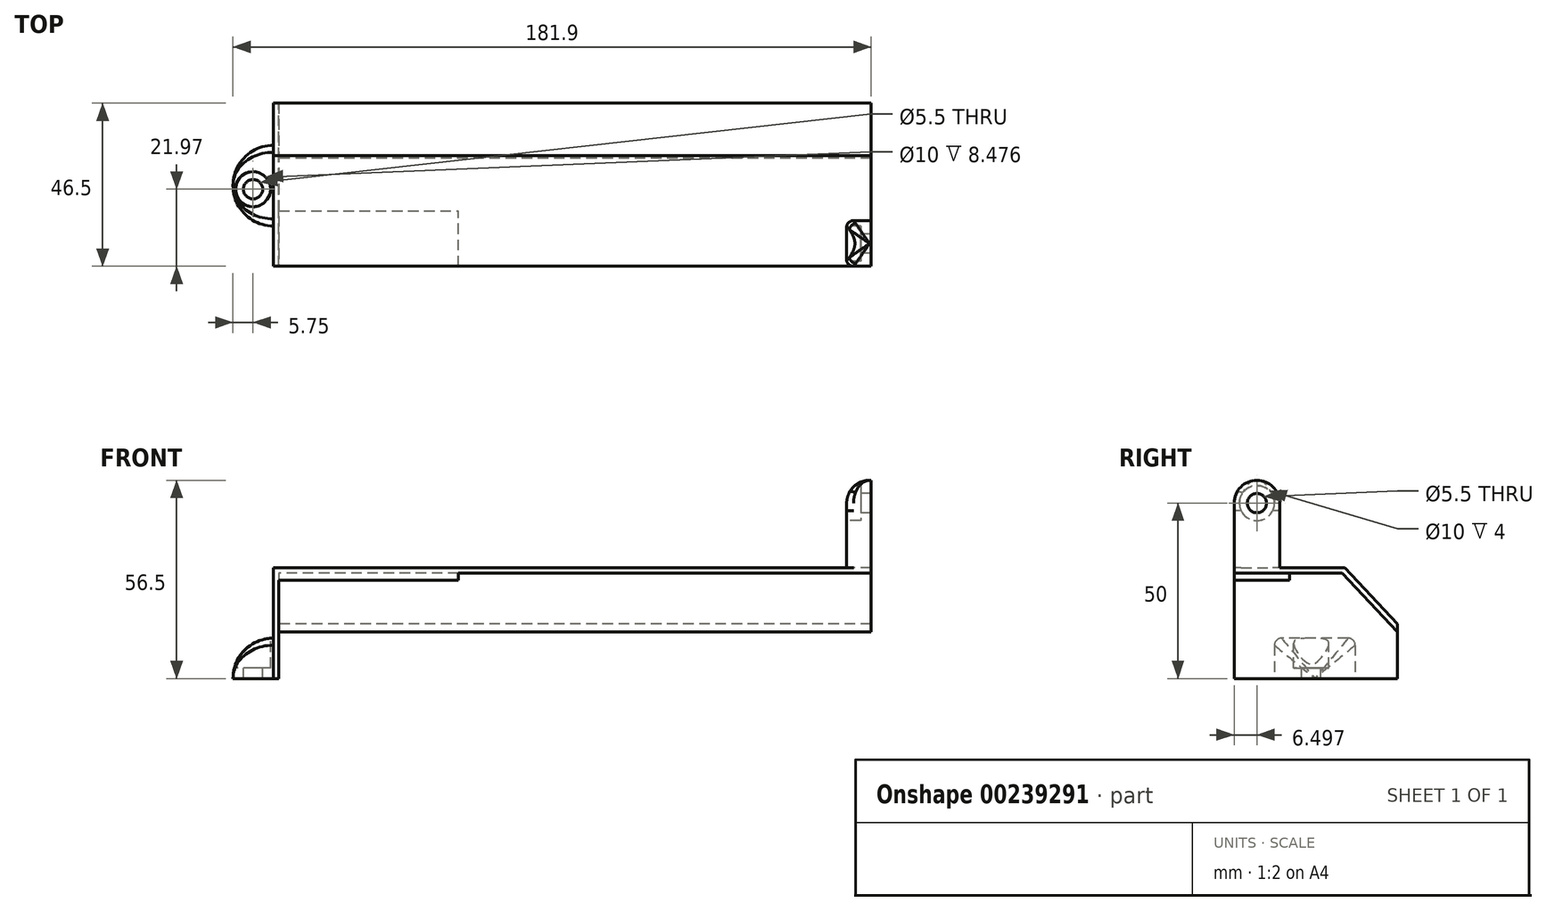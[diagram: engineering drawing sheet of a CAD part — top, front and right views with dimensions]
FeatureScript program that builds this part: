
annotation { "Feature Type Name" : "Feature", "Feature Type Description" : "" }
export const myFeature = defineFeature(function(context is Context, id is Id, definition is map)
    precondition{}
    {
        {
            var Q0;
            Q0=qCreatedBy(makeId("Right.planeOp"),FACE);
            var sketch = newSketch(context, id + "F0", { "sketchPlane" : qUnion([Q0])});
            skLineSegment(sketch, "E0", {"start": v(-21.97, 0) * mm, "end": v(-21.97, 31.6) * mm});
            skLineSegment(sketch, "E1", {"start": v(-21.97, 31.6) * mm, "end": v(-6.47, 31.6) * mm});
            skLineSegment(sketch, "E2", {"start": v(-6.47, 31.6) * mm, "end": v(9.53, 31.6) * mm});
            skLineSegment(sketch, "E3", {"start": v(9.53, 31.6) * mm, "end": v(24.53, 15.6) * mm});
            skLineSegment(sketch, "E4", {"start": v(24.53, 15.6) * mm, "end": v(24.53, 0) * mm});
            skLineSegment(sketch, "E5", {"start": v(24.53, 0) * mm, "end": v(-21.97, 0) * mm});
            skSolve(sketch);
        }
        {
            var Q0;
            Q0=makeQuery(id+"F0.imprint","IMPRINT",FACE,{"disambiguationData":[TD([[makeQuery(id+"F0.imprint","IMPRINT",EDGE,{"derivedFrom":sQuery(id+"F0.wireOp",EDGE,"E0")}),-1.0]])]});
            extrude(context, id + "F1", {"entities" : qUnion([Q0]), "depth" : 170.4 * mm});
        }
        {
            var Q0;
            Q0=makeQuery(id+"F1.opExtrude","SWEPT_FACE",FACE,{"disambiguationData":[OSD([sQuery(id+"F0.wireOp",EDGE,"E5")])]});
            var Q1;
            Q1=makeQuery(id+"F1.opExtrude","SWEPT_FACE",FACE,{"disambiguationData":[OSD([sQuery(id+"F0.wireOp",EDGE,"E4")])]});
            var Q2;
            Q2=makeQuery(id+"F1.opExtrude","SWEPT_FACE",FACE,{"disambiguationData":[OSD([sQuery(id+"F0.wireOp",EDGE,"E0")])]});
            var Q3;
            Q3=makeQuery(id+"F1.opExtrude","CAP_FACE",FACE,{"disambiguationData":[OSD([sQuery(id+"F0.wireOp",EDGE,"E0"),sQuery(id+"F0.wireOp",EDGE,"E1"),sQuery(id+"F0.wireOp",EDGE,"E2"),sQuery(id+"F0.wireOp",EDGE,"E3"),sQuery(id+"F0.wireOp",EDGE,"E4"),sQuery(id+"F0.wireOp",EDGE,"E5")])],"isStart":false});
            shell(context, id + "F2", {"entities" : qUnion([Q0, Q1, Q2, Q3]), "thickness" : 1.6 * mm});
        }
        {
            var Q0;
            Q0=makeQuery(id+"F2.opShell","OFFSET_FACE",FACE,{"disambiguationData":[OSD([sQuery(id+"F0.wireOp",EDGE,"E1"),sQuery(id+"F0.wireOp",EDGE,"E2")])]});
            var sketch = newSketch(context, id + "F3", { "sketchPlane" : qUnion([Q0])});
            skLineSegment(sketch, "E6.bottom", {"start": v(1.6, 21.97) * mm, "end": v(52.8, 21.97) * mm});
            skLineSegment(sketch, "E6.top", {"start": v(1.6, 6.17) * mm, "end": v(52.8, 6.17) * mm});
            skLineSegment(sketch, "E6.left", {"start": v(1.6, 21.97) * mm, "end": v(1.6, 6.17) * mm});
            skLineSegment(sketch, "E6.right", {"start": v(52.8, 21.97) * mm, "end": v(52.8, 6.17) * mm});
            skSolve(sketch);
        }
        {
            var Q0;
            Q0=makeQuery(id+"F3.imprint","IMPRINT",FACE,{"disambiguationData":[TD([[makeQuery(id+"F3.imprint","IMPRINT",EDGE,{"derivedFrom":sQuery(id+"F3.wireOp",EDGE,"E6.bottom")}),1.0]])]});
            extrude(context, id + "F4", {"entities" : qUnion([Q0]), "operationType" : NewBodyOperationType.ADD, "depth" : 2 * mm});
        }
        {
            var Q0;
            Q0=makeQuery(id+"F0.imprint","IMPRINT",FACE,{"disambiguationData":[TD([[makeQuery(id+"F0.imprint","IMPRINT",EDGE,{"derivedFrom":sQuery(id+"F0.wireOp",EDGE,"E0")}),-1.0]])]});
            var sketch = newSketch(context, id + "F5", { "sketchPlane" : qUnion([Q0])});
            skLineSegment(sketch, "E7.bottom", {"start": v(12.53, 11.5) * mm, "end": v(-10.47, 11.5) * mm});
            skLineSegment(sketch, "E7.top", {"start": v(12.53, 0) * mm, "end": v(-10.47, 0) * mm});
            skLineSegment(sketch, "E7.left", {"start": v(12.53, 11.5) * mm, "end": v(12.53, 0) * mm});
            skLineSegment(sketch, "E7.right", {"start": v(-10.47, 11.5) * mm, "end": v(-10.47, 0) * mm});
            skSolve(sketch);
        }
        {
            var Q0;
            Q0=makeQuery(id+"F5.imprint","IMPRINT",FACE,{"disambiguationData":[TD([[makeQuery(id+"F5.imprint","IMPRINT",EDGE,{"derivedFrom":sQuery(id+"F5.wireOp",EDGE,"E7.bottom")}),1.0]])]});
            extrude(context, id + "F6", {"entities" : qUnion([Q0]), "operationType" : NewBodyOperationType.ADD, "oppositeDirection" : true, "depth" : 11.5 * mm});
        }
        {
            var Q0;
            Q0=qCreatedBy(makeId("Top.planeOp"),FACE);
            cPlane(context, id + "F7", {"entities" : qUnion([Q0]), "cplaneType" : CPlaneType.OFFSET, "offset" : 11.5 * mm, "width" : 150 * mm, "height" : 150 * mm});
        }
        {
            var Q0;
            Q0=qCreatedBy(id+"F7.planeOp",FACE);
            var sketch = newSketch(context, id + "F8", { "sketchPlane" : qUnion([Q0])});
            skPoint(sketch, "E8", {"position": v(-5.75, 0) * mm});
            skSolve(sketch);
        }
        {
            var Q0;
            Q0=makeQuery(id+"F1.opExtrude","SWEPT_FACE",FACE,{"disambiguationData":[OSD([sQuery(id+"F0.wireOp",EDGE,"E1"),sQuery(id+"F0.wireOp",EDGE,"E2")])]});
            var sketch = newSketch(context, id + "F9", { "sketchPlane" : qUnion([Q0])});
            skLineSegment(sketch, "E9.bottom", {"start": v(170.4, -21.97) * mm, "end": v(163.4, -21.97) * mm});
            skLineSegment(sketch, "E9.top", {"start": v(170.4, -8.97) * mm, "end": v(163.4, -8.97) * mm});
            skLineSegment(sketch, "E9.left", {"start": v(170.4, -21.97) * mm, "end": v(170.4, -8.97) * mm});
            skLineSegment(sketch, "E9.right", {"start": v(163.4, -21.97) * mm, "end": v(163.4, -8.97) * mm});
            skSolve(sketch);
        }
        {
            var Q0;
            Q0=makeQuery(id+"F9.imprint","IMPRINT",FACE,{"disambiguationData":[TD([[makeQuery(id+"F9.imprint","IMPRINT",EDGE,{"derivedFrom":sQuery(id+"F9.wireOp",EDGE,"E9.bottom")}),-1.0]])]});
            extrude(context, id + "F10", {"entities" : qUnion([Q0]), "operationType" : NewBodyOperationType.ADD, "depth" : 24.9 * mm});
        }
        {
            var Q0;
            Q0=makeQuery(id+"F6.opExtrude","CAP_EDGE",EDGE,{"disambiguationData":[OSD([sQuery(id+"F5.wireOp",EDGE,"E7.bottom")])],"isStart":false});
            var Q1;
            Q1=makeQuery(id+"F6.opExtrude","CAP_EDGE",EDGE,{"disambiguationData":[OSD([sQuery(id+"F5.wireOp",EDGE,"E7.right")])],"isStart":false});
            var Q2;
            Q2=makeQuery(id+"F6.opExtrude","CAP_EDGE",EDGE,{"disambiguationData":[OSD([sQuery(id+"F5.wireOp",EDGE,"E7.left")])],"isStart":false});
            fillet(context, id + "F11", {"entities" : qUnion([Q0, Q1, Q2]), "radius" : 11.5 * mm, "tangentPropagation" : true, "allowEdgeOverflow" : false});
        }
        {
            var Q0;
            Q0=makeQuery(id+"F10.boolean.opBoolean","MERGE",FACE,{"derivedFrom":[makeQuery(id+"F1.opExtrude","CAP_FACE",FACE,{"disambiguationData":[OSD([sQuery(id+"F0.wireOp",EDGE,"E0"),sQuery(id+"F0.wireOp",EDGE,"E1"),sQuery(id+"F0.wireOp",EDGE,"E2"),sQuery(id+"F0.wireOp",EDGE,"E3"),sQuery(id+"F0.wireOp",EDGE,"E4"),sQuery(id+"F0.wireOp",EDGE,"E5")])],"isStart":false}),makeQuery(id+"F10.opExtrude","SWEPT_FACE",FACE,{"disambiguationData":[OSD([sQuery(id+"F9.wireOp",EDGE,"E9.left")])]})]});
            cPlane(context, id + "F12", {"entities" : qUnion([Q0]), "cplaneType" : CPlaneType.OFFSET, "offset" : 11.5 * mm, "oppositeDirection" : true, "width" : 150 * mm, "height" : 150 * mm});
        }
        {
            var Q0;
            Q0=qCreatedBy(id+"F12.planeOp",FACE);
            var sketch = newSketch(context, id + "F13", { "sketchPlane" : qUnion([Q0])});
            skPoint(sketch, "E10", {"position": v(-15.47, 50) * mm});
            skSolve(sketch);
        }
        {
            var Q0;
            Q0=sQuery(id+"F8.wireOp",VERTEX,"E8");
            var Q1;
            Q1=makeQuery(id+"F1.opExtrude","SWEPT_BODY",BODY,{"disambiguationData":[OSD([sQuery(id+"F0.wireOp",EDGE,"E0"),sQuery(id+"F0.wireOp",EDGE,"E1"),sQuery(id+"F0.wireOp",EDGE,"E2"),sQuery(id+"F0.wireOp",EDGE,"E3"),sQuery(id+"F0.wireOp",EDGE,"E4"),sQuery(id+"F0.wireOp",EDGE,"E5")])]});
            hole(context, id + "F14", {"style" : HoleStyle.C_BORE, "endStyle" : HoleEndStyle.THROUGH, "holeDiameter" : 5.5 * mm, "cBoreDiameter" : 10 * mm, "cBoreDepth" : 8.5 * mm, "startFromSketch" : true, "locations" : qUnion([Q0]), "scope" : qUnion([Q1]), "isTappedThrough" : true});
        }
        {
            var Q0;
            Q0=sQuery(id+"F13.wireOp",VERTEX,"E10");
            var Q1;
            Q1=makeQuery(id+"F1.opExtrude","SWEPT_BODY",BODY,{"disambiguationData":[OSD([sQuery(id+"F0.wireOp",EDGE,"E0"),sQuery(id+"F0.wireOp",EDGE,"E1"),sQuery(id+"F0.wireOp",EDGE,"E2"),sQuery(id+"F0.wireOp",EDGE,"E3"),sQuery(id+"F0.wireOp",EDGE,"E4"),sQuery(id+"F0.wireOp",EDGE,"E5")])]});
            hole(context, id + "F15", {"style" : HoleStyle.C_BORE, "endStyle" : HoleEndStyle.THROUGH, "oppositeDirection" : true, "holeDiameter" : 5.5 * mm, "cBoreDiameter" : 10 * mm, "cBoreDepth" : 8.5 * mm, "startFromSketch" : true, "locations" : qUnion([Q0]), "scope" : qUnion([Q1]), "isTappedThrough" : true});
        }
        {
            var Q0;
            Q0=makeQuery(id+"F10.opExtrude","CAP_EDGE",EDGE,{"disambiguationData":[OSD([sQuery(id+"F9.wireOp",EDGE,"E9.bottom")])],"isStart":false});
            var Q1;
            Q1=makeQuery(id+"F10.opExtrude","CAP_EDGE",EDGE,{"disambiguationData":[OSD([sQuery(id+"F9.wireOp",EDGE,"E9.top")])],"isStart":false});
            var Q2;
            Q2=makeQuery(id+"F10.opExtrude","CAP_EDGE",EDGE,{"disambiguationData":[OSD([sQuery(id+"F9.wireOp",EDGE,"E9.right")])],"isStart":false});
            fillet(context, id + "F16", {"entities" : qUnion([Q0, Q1, Q2]), "radius" : 6.5 * mm, "tangentPropagation" : true, "allowEdgeOverflow" : false});
        }
        {
            var Q0;
            Q0=makeQuery(id+"F10.opExtrude","SWEPT_EDGE",EDGE,{"disambiguationData":[OSD([sQuery(id+"F0.wireOp",EDGE,"E0"),sQuery(id+"F0.wireOp",EDGE,"E1"),sQuery(id+"F9.wireOp",EDGE,"E9.bottom"),sQuery(id+"F9.wireOp",EDGE,"E9.right")])]});
            var Q1;
            Q1=makeQuery(id+"F10.opExtrude","SWEPT_EDGE",EDGE,{"disambiguationData":[OSD([sQuery(id+"F9.wireOp",EDGE,"E9.top"),sQuery(id+"F9.wireOp",EDGE,"E9.right")])]});
            var Q2;
            Q2=makeQuery(id+"F11.opFillet","BLEND_EDGE",EDGE,{"blendedFrom":[makeQuery(id+"F6.opExtrude","CAP_EDGE",EDGE,{"disambiguationData":[OSD([sQuery(id+"F5.wireOp",EDGE,"E7.bottom")])],"isStart":false}),makeQuery(id+"F6.opExtrude","CAP_EDGE",EDGE,{"disambiguationData":[OSD([sQuery(id+"F5.wireOp",EDGE,"E7.left")])],"isStart":false})],"blendedInto":[]});
            var Q3;
            Q3=makeQuery(id+"F11.opFillet","BLEND_EDGE",EDGE,{"blendedFrom":[makeQuery(id+"F6.opExtrude","CAP_EDGE",EDGE,{"disambiguationData":[OSD([sQuery(id+"F5.wireOp",EDGE,"E7.bottom")])],"isStart":false}),makeQuery(id+"F6.opExtrude","CAP_EDGE",EDGE,{"disambiguationData":[OSD([sQuery(id+"F5.wireOp",EDGE,"E7.right")])],"isStart":false})],"blendedInto":[]});
            fillet(context, id + "F17", {"entities" : qUnion([Q0, Q1, Q2, Q3]), "radius" : 2 * mm, "tangentPropagation" : true, "allowEdgeOverflow" : false});
        }
    });
